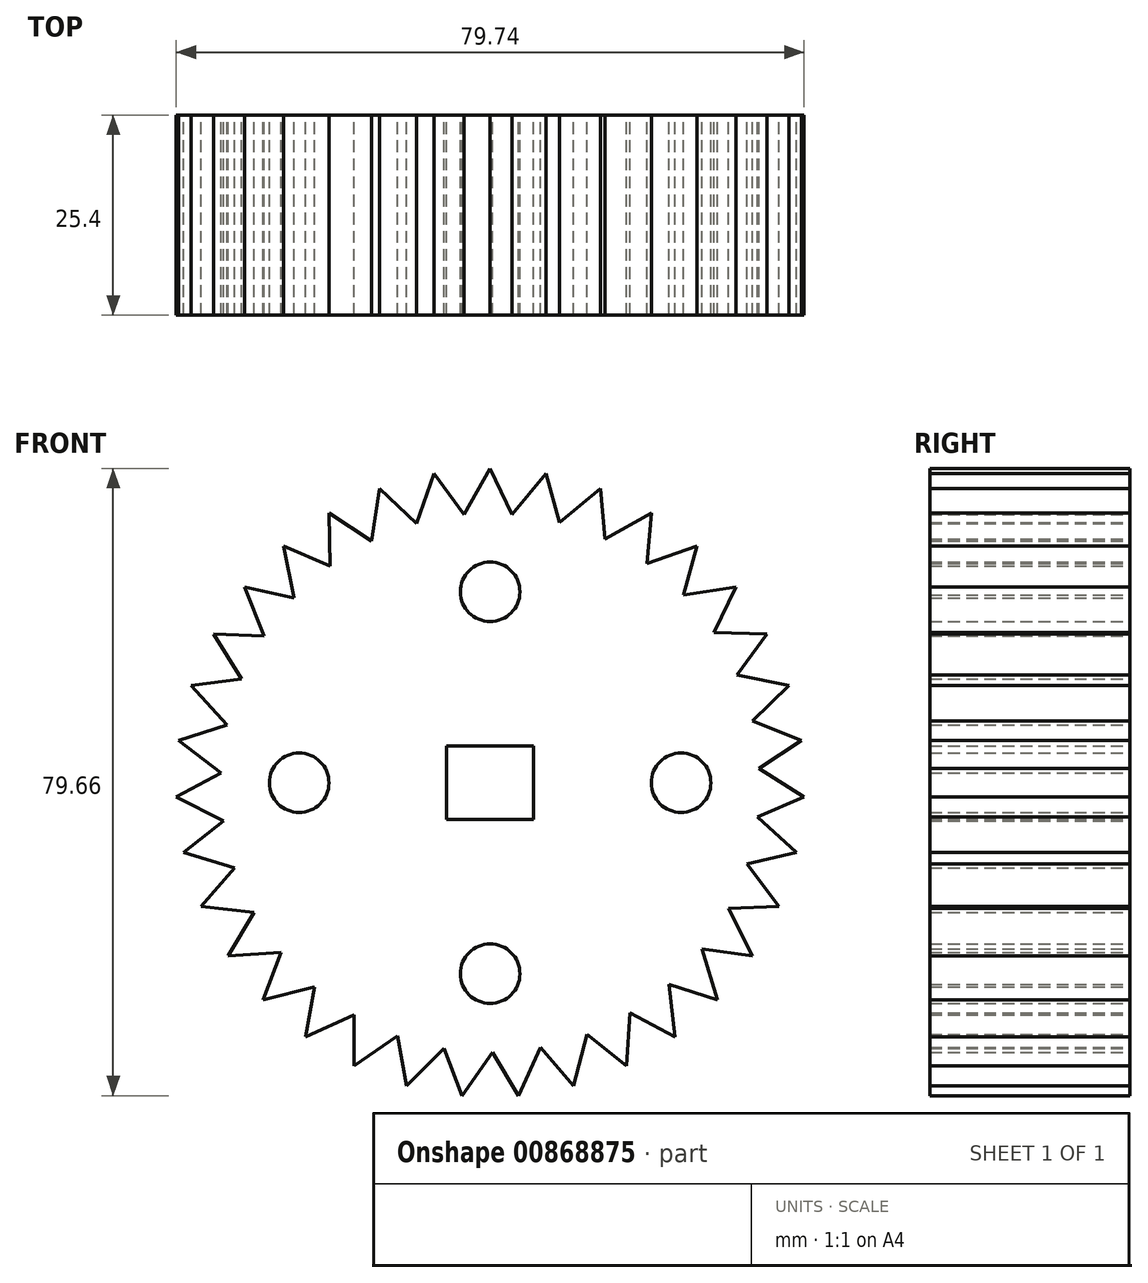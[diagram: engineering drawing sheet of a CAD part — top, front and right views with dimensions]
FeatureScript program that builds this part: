
annotation { "Feature Type Name" : "Feature", "Feature Type Description" : "" }
export const myFeature = defineFeature(function(context is Context, id is Id, definition is map)
    precondition{}
    {
        {
            var Q0;
            Q0=qCreatedBy(makeId("Front.planeOp"),FACE);
            var sketch = newSketch(context, id + "F0", { "sketchPlane" : qUnion([Q0])});
            skLineSegment(sketch, "E0.bottom", {"start": v(5.53, 4.68) * mm, "end": v(-5.53, 4.68) * mm});
            skLineSegment(sketch, "E0.top", {"start": v(5.53, -4.68) * mm, "end": v(-5.53, -4.68) * mm});
            skLineSegment(sketch, "E0.left", {"start": v(5.53, 4.68) * mm, "end": v(5.53, -4.68) * mm});
            skLineSegment(sketch, "E0.right", {"start": v(-5.53, 4.68) * mm, "end": v(-5.53, -4.68) * mm});
            skPoint(sketch, "E0.middle", {"position": v(0, 0) * mm});
            skLineSegment(sketch, "E1.bottom", {"start": v(9.22, 8.65) * mm, "end": v(-9.22, 8.65) * mm});
            skLineSegment(sketch, "E1.top", {"start": v(9.22, -8.65) * mm, "end": v(-9.22, -8.65) * mm});
            skLineSegment(sketch, "E1.left", {"start": v(9.22, 8.65) * mm, "end": v(9.22, -8.65) * mm});
            skLineSegment(sketch, "E1.right", {"start": v(-9.22, 8.65) * mm, "end": v(-9.22, -8.65) * mm});
            skLineSegment(sketch, "E2", {"start": v(-2.98, 8.65) * mm, "end": v(-2.98, 16.88) * mm});
            skLineSegment(sketch, "E3", {"start": v(2.98, 8.65) * mm, "end": v(2.98, 16.88) * mm});
            skCircle(sketch, "E4", {"center": v(0, 24.26) * mm, "radius": 3.78 * mm});
            skLineSegment(sketch, "E5.1.0", {"start": v(-8.65, 2.98) * mm, "end": v(-16.88, 2.98) * mm});
            skLineSegment(sketch, "E5.1.1", {"start": v(-8.65, -2.98) * mm, "end": v(-16.88, -2.98) * mm});
            skCircle(sketch, "E5.1.2", {"center": v(-24.26, 0) * mm, "radius": 3.78 * mm});
            skLineSegment(sketch, "E5.2.0", {"start": v(-2.98, -8.65) * mm, "end": v(-2.98, -16.88) * mm});
            skLineSegment(sketch, "E5.2.1", {"start": v(2.98, -8.65) * mm, "end": v(2.98, -16.88) * mm});
            skCircle(sketch, "E5.2.2", {"center": v(0, -24.26) * mm, "radius": 3.78 * mm});
            skLineSegment(sketch, "E5.3.0", {"start": v(8.65, -2.98) * mm, "end": v(16.88, -2.98) * mm});
            skLineSegment(sketch, "E5.3.1", {"start": v(8.65, 2.98) * mm, "end": v(16.88, 2.98) * mm});
            skCircle(sketch, "E5.3.2", {"center": v(24.26, 0) * mm, "radius": 3.78 * mm});
            skCircle(sketch, "E6", {"center": v(0, 23.4) * mm, "radius": 7.16 * mm});
            skPoint(sketch, "E6.third.point", {"position": v(0, 30.56) * mm});
            skCircle(sketch, "E7.1.0", {"center": v(-23.4, 0) * mm, "radius": 7.16 * mm});
            skCircle(sketch, "E7.2.0", {"center": v(0, -23.4) * mm, "radius": 7.16 * mm});
            skCircle(sketch, "E7.3.0", {"center": v(23.4, 0) * mm, "radius": 7.16 * mm});
            skCircle(sketch, "E8", {"center": v(0, 0) * mm, "radius": 33.5 * mm});
            skLineSegment(sketch, "E9", {"start": v(-3.78, 33.28) * mm, "end": v(0, 39.91) * mm});
            skLineSegment(sketch, "E10", {"start": v(0, 39.91) * mm, "end": v(3.16, 33.34) * mm});
            skLineSegment(sketch, "E11.1.0", {"start": v(-7.13, 39.27) * mm, "end": v(-2.84, 33.37) * mm});
            skLineSegment(sketch, "E11.1.1", {"start": v(-9.66, 32.07) * mm, "end": v(-7.13, 39.27) * mm});
            skLineSegment(sketch, "E11.2.0", {"start": v(-14.02, 37.37) * mm, "end": v(-8.76, 32.33) * mm});
            skLineSegment(sketch, "E11.2.1", {"start": v(-15.24, 29.83) * mm, "end": v(-14.02, 37.37) * mm});
            skLineSegment(sketch, "E11.3.0", {"start": v(-20.47, 34.26) * mm, "end": v(-14.39, 30.25) * mm});
            skLineSegment(sketch, "E11.3.1", {"start": v(-20.32, 26.63) * mm, "end": v(-20.47, 34.26) * mm});
            skLineSegment(sketch, "E11.4.0", {"start": v(-26.26, 30.06) * mm, "end": v(-19.56, 27.2) * mm});
            skLineSegment(sketch, "E11.4.1", {"start": v(-24.74, 22.57) * mm, "end": v(-26.26, 30.06) * mm});
            skLineSegment(sketch, "E11.5.0", {"start": v(-31.2, 24.89) * mm, "end": v(-24.1, 23.26) * mm});
            skLineSegment(sketch, "E11.5.1", {"start": v(-28.38, 17.8) * mm, "end": v(-31.2, 24.89) * mm});
            skLineSegment(sketch, "E11.6.0", {"start": v(-35.15, 18.91) * mm, "end": v(-27.86, 18.59) * mm});
            skLineSegment(sketch, "E11.6.1", {"start": v(-31.1, 12.44) * mm, "end": v(-35.15, 18.91) * mm});
            skLineSegment(sketch, "E11.7.0", {"start": v(-37.96, 12.33) * mm, "end": v(-30.74, 13.31) * mm});
            skLineSegment(sketch, "E11.7.1", {"start": v(-32.82, 6.69) * mm, "end": v(-37.96, 12.33) * mm});
            skLineSegment(sketch, "E11.8.0", {"start": v(-39.55, 5.36) * mm, "end": v(-32.62, 7.6) * mm});
            skLineSegment(sketch, "E11.8.1", {"start": v(-33.49, 0.72) * mm, "end": v(-39.55, 5.36) * mm});
            skLineSegment(sketch, "E11.9.0", {"start": v(-39.87, -1.8) * mm, "end": v(-33.45, 1.66) * mm});
            skLineSegment(sketch, "E11.9.1", {"start": v(-33.08, -5.27) * mm, "end": v(-39.87, -1.8) * mm});
            skLineSegment(sketch, "E12.2.10.0", {"start": v(-38.91, -8.88) * mm, "end": v(-33.21, -4.34) * mm});
            skLineSegment(sketch, "E12.3.10.0", {"start": v(-31.6, -11.1) * mm, "end": v(-38.91, -8.88) * mm});
            skLineSegment(sketch, "E12.2.11.0", {"start": v(-36.7, -15.69) * mm, "end": v(-31.9, -10.2) * mm});
            skLineSegment(sketch, "E12.3.11.0", {"start": v(-29.12, -16.56) * mm, "end": v(-36.7, -15.69) * mm});
            skLineSegment(sketch, "E12.2.12.0", {"start": v(-33.31, -21.99) * mm, "end": v(-29.57, -15.73) * mm});
            skLineSegment(sketch, "E12.3.12.0", {"start": v(-25.7, -21.5) * mm, "end": v(-33.31, -21.99) * mm});
            skLineSegment(sketch, "E12.2.13.0", {"start": v(-28.85, -27.58) * mm, "end": v(-26.29, -20.76) * mm});
            skLineSegment(sketch, "E12.3.13.0", {"start": v(-21.44, -25.73) * mm, "end": v(-28.85, -27.58) * mm});
            skLineSegment(sketch, "E12.2.14.0", {"start": v(-23.46, -32.3) * mm, "end": v(-22.16, -25.12) * mm});
            skLineSegment(sketch, "E12.3.14.0", {"start": v(-16.5, -29.15) * mm, "end": v(-23.46, -32.3) * mm});
            skLineSegment(sketch, "E12.2.15.0", {"start": v(-17.32, -35.96) * mm, "end": v(-17.32, -28.67) * mm});
            skLineSegment(sketch, "E12.3.15.0", {"start": v(-11.03, -31.63) * mm, "end": v(-17.32, -35.96) * mm});
            skLineSegment(sketch, "E12.2.16.0", {"start": v(-10.62, -38.47) * mm, "end": v(-11.92, -31.3) * mm});
            skLineSegment(sketch, "E12.3.16.0", {"start": v(-5.2, -33.09) * mm, "end": v(-10.62, -38.47) * mm});
            skLineSegment(sketch, "E12.2.17.0", {"start": v(-3.58, -39.75) * mm, "end": v(-6.14, -32.93) * mm});
            skLineSegment(sketch, "E12.3.17.0", {"start": v(0.78, -33.48) * mm, "end": v(-3.58, -39.75) * mm});
            skLineSegment(sketch, "E12.2.18.0", {"start": v(3.58, -39.75) * mm, "end": v(-0.16, -33.5) * mm});
            skLineSegment(sketch, "E12.3.18.0", {"start": v(6.75, -32.8) * mm, "end": v(3.58, -39.75) * mm});
            skLineSegment(sketch, "E12.2.19.0", {"start": v(10.62, -38.47) * mm, "end": v(5.82, -32.98) * mm});
            skLineSegment(sketch, "E12.3.19.0", {"start": v(12.5, -31.07) * mm, "end": v(10.62, -38.47) * mm});
            skLineSegment(sketch, "E12.2.20.0", {"start": v(17.32, -35.96) * mm, "end": v(11.62, -31.41) * mm});
            skLineSegment(sketch, "E12.3.20.0", {"start": v(17.85, -28.34) * mm, "end": v(17.32, -35.96) * mm});
            skLineSegment(sketch, "E12.2.21.0", {"start": v(23.46, -32.3) * mm, "end": v(17.04, -28.83) * mm});
            skLineSegment(sketch, "E12.3.21.0", {"start": v(22.62, -24.7) * mm, "end": v(23.46, -32.3) * mm});
            skLineSegment(sketch, "E12.2.22.0", {"start": v(28.85, -27.58) * mm, "end": v(21.92, -25.33) * mm});
            skLineSegment(sketch, "E12.3.22.0", {"start": v(26.67, -20.26) * mm, "end": v(28.85, -27.58) * mm});
            skLineSegment(sketch, "E12.2.23.0", {"start": v(33.31, -21.99) * mm, "end": v(26.09, -21) * mm});
            skLineSegment(sketch, "E12.3.23.0", {"start": v(29.86, -15.18) * mm, "end": v(33.31, -21.99) * mm});
            skLineSegment(sketch, "E12.2.24.0", {"start": v(36.7, -15.69) * mm, "end": v(29.42, -16.01) * mm});
            skLineSegment(sketch, "E12.3.24.0", {"start": v(32.09, -9.6) * mm, "end": v(36.7, -15.69) * mm});
            skLineSegment(sketch, "E12.2.25.0", {"start": v(38.91, -8.88) * mm, "end": v(31.8, -10.5) * mm});
            skLineSegment(sketch, "E12.3.25.0", {"start": v(33.29, -3.72) * mm, "end": v(38.91, -8.88) * mm});
            skLineSegment(sketch, "E12.2.26.0", {"start": v(39.87, -1.8) * mm, "end": v(33.17, -4.65) * mm});
            skLineSegment(sketch, "E12.3.26.0", {"start": v(33.42, 2.29) * mm, "end": v(39.87, -1.8) * mm});
            skLineSegment(sketch, "E12.2.27.0", {"start": v(39.55, 5.36) * mm, "end": v(33.47, 1.34) * mm});
            skLineSegment(sketch, "E12.3.27.0", {"start": v(32.47, 8.22) * mm, "end": v(39.55, 5.36) * mm});
            skLineSegment(sketch, "E12.2.28.0", {"start": v(37.96, 12.33) * mm, "end": v(32.69, 7.3) * mm});
            skLineSegment(sketch, "E12.3.28.0", {"start": v(30.48, 13.88) * mm, "end": v(37.96, 12.33) * mm});
            skLineSegment(sketch, "E12.2.29.0", {"start": v(35.15, 18.91) * mm, "end": v(30.86, 13.02) * mm});
            skLineSegment(sketch, "E12.3.29.0", {"start": v(27.51, 19.1) * mm, "end": v(35.15, 18.91) * mm});
            skLineSegment(sketch, "E13.2.30.0", {"start": v(31.2, 24.89) * mm, "end": v(28.04, 18.32) * mm});
            skLineSegment(sketch, "E13.3.30.0", {"start": v(23.66, 23.7) * mm, "end": v(31.2, 24.89) * mm});
            skLineSegment(sketch, "E13.2.31.0", {"start": v(26.26, 30.06) * mm, "end": v(24.32, 23.03) * mm});
            skLineSegment(sketch, "E13.3.31.0", {"start": v(19.05, 27.55) * mm, "end": v(26.26, 30.06) * mm});
            skLineSegment(sketch, "E13.2.32.0", {"start": v(20.47, 34.26) * mm, "end": v(19.82, 27) * mm});
            skLineSegment(sketch, "E13.3.32.0", {"start": v(13.82, 30.5) * mm, "end": v(20.47, 34.26) * mm});
            skLineSegment(sketch, "E13.2.33.0", {"start": v(14.02, 37.37) * mm, "end": v(14.68, 30.1) * mm});
            skLineSegment(sketch, "E13.3.33.0", {"start": v(8.15, 32.49) * mm, "end": v(14.02, 37.37) * mm});
            skLineSegment(sketch, "E13.2.34.0", {"start": v(7.13, 39.27) * mm, "end": v(9.07, 32.24) * mm});
            skLineSegment(sketch, "E13.3.34.0", {"start": v(2.22, 33.42) * mm, "end": v(7.13, 39.27) * mm});
            skSolve(sketch);
        }
        {
            var Q0;
            Q0=qSketchRegion(id+"F0",true);
            var Q1;
            {var subQ23=sQuery(id+"F0.wireOp",EDGE,"E2");Q1=makeQuery(id+"F0.imprint","IMPRINT",FACE,{"disambiguationData":[TD([[makeQuery(id+"F0.imprint","IMPRINT",EDGE,{"derivedFrom":subQ23}),1.0]])]});}
            var Q2;
            Q2=makeQuery(id+"F0.imprint","IMPRINT",FACE,{"disambiguationData":[TD([[makeQuery(id+"F0.imprint","IMPRINT",EDGE,{"derivedFrom":sQuery(id+"F0.wireOp",EDGE,"E0.bottom")}),-1.0]])]});
            var Q3;
            {var subQ0=sQuery(id+"F0.wireOp",EDGE,"E5.1.0");var subQ1=sQuery(id+"F0.wireOp",EDGE,"E1.right");var subQ2=makeQuery(id+"F0.imprint","INTERSECT",VERTEX,{"derivedFrom":[subQ1,subQ0]});Q3=makeQuery(id+"F0.imprint","IMPRINT",FACE,{"disambiguationData":[TD([[makeQuery(id+"F0.imprint","IMPRINT",EDGE,{"disambiguationData":[TD([[subQ2,-1.0]])],"derivedFrom":subQ1}),-1.0]])]});}
            var Q4;
            Q4=makeQuery(id+"F0.imprint","IMPRINT",FACE,{"disambiguationData":[TD([[makeQuery(id+"F0.imprint","IMPRINT",EDGE,{"derivedFrom":sQuery(id+"F0.wireOp",EDGE,"E5.1.2")}),-1.0]])]});
            var Q5;
            {var subQ0=sQuery(id+"F0.wireOp",EDGE,"E5.2.0");Q5=makeQuery(id+"F0.imprint","IMPRINT",FACE,{"disambiguationData":[TD([[makeQuery(id+"F0.imprint","IMPRINT",EDGE,{"derivedFrom":subQ0}),1.0]])]});}
            var Q6;
            {var subQ0=sQuery(id+"F0.wireOp",EDGE,"E5.3.1");var subQ1=sQuery(id+"F0.wireOp",EDGE,"E1.left");var subQ2=makeQuery(id+"F0.imprint","INTERSECT",VERTEX,{"derivedFrom":[subQ1,subQ0]});Q6=makeQuery(id+"F0.imprint","IMPRINT",FACE,{"disambiguationData":[TD([[makeQuery(id+"F0.imprint","IMPRINT",EDGE,{"disambiguationData":[TD([[subQ2,-1.0]])],"derivedFrom":subQ1}),1.0]])]});}
            var Q7;
            {var subQ0=sQuery(id+"F0.wireOp",EDGE,"E2");Q7=makeQuery(id+"F0.imprint","IMPRINT",FACE,{"disambiguationData":[TD([[makeQuery(id+"F0.imprint","IMPRINT",EDGE,{"derivedFrom":subQ0}),-1.0]])]});}
            var Q8;
            Q8=makeQuery(id+"F0.imprint","IMPRINT",FACE,{"disambiguationData":[TD([[makeQuery(id+"F0.imprint","IMPRINT",EDGE,{"derivedFrom":sQuery(id+"F0.wireOp",EDGE,"E4")}),-1.0]])]});
            var Q9;
            Q9=makeQuery(id+"F0.imprint","IMPRINT",FACE,{"disambiguationData":[TD([[makeQuery(id+"F0.imprint","IMPRINT",EDGE,{"derivedFrom":sQuery(id+"F0.wireOp",EDGE,"E5.2.2")}),-1.0]])]});
            var Q10;
            Q10=makeQuery(id+"F0.imprint","IMPRINT",FACE,{"disambiguationData":[TD([[makeQuery(id+"F0.imprint","IMPRINT",EDGE,{"derivedFrom":sQuery(id+"F0.wireOp",EDGE,"E5.3.2")}),-1.0]])]});
            extrude(context, id + "F1", {"entities" : qUnion([Q0, Q1, Q2, Q3, Q4, Q5, Q6, Q7, Q8, Q9, Q10]), "depth" : 25.4 * mm, "offsetDistance" : 25.4 * mm});
        }
    });
